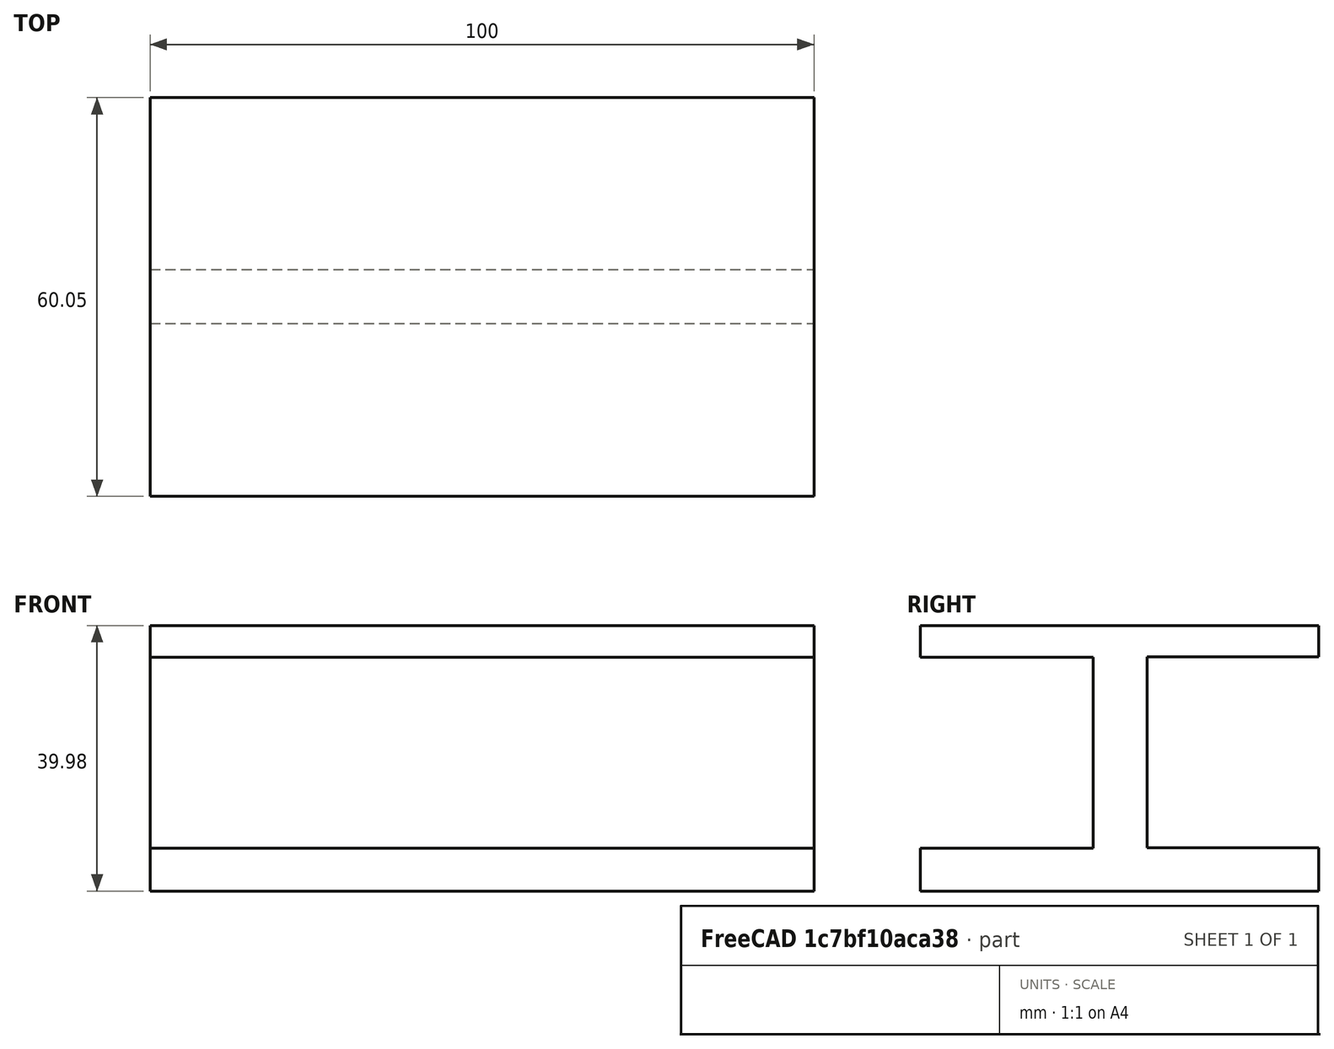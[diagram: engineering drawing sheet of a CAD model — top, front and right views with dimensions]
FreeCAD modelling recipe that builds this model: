
FCSTD DOCUMENT  (FreeCAD 0.21R33694 (Git))
Label: OJT1_T18R01_biga
License: All rights reserved
LicenseURL: https://en.wikipedia.org/wiki/All_rights_reserved
objects: Sketcher::SketchObject×1, PartDesign::Pad×1, PartDesign::Body×1
note: 4 computed .brp shape members not serialized (recipe doc carries the construction recipe); baked Part::Feature solids carry a one-line shape summary decoded from their .brp

FEATURE [Sketcher::SketchObject] Sketch
  FullyConstrained = false
  MapMode = 5
  Placement = pos=(0,0,0) rot=(0.57735,0.57735,0.57735;2.0944rad)
  Support = -> [YZ_Plane]
  sketch-geometry (12):
    g0: LineSegment StartX=-30.05 StartY=0 StartZ=0 EndX=29.9884 EndY=0 EndZ=0
    g1: LineSegment StartX=29.9884 StartY=0 StartZ=0 EndX=29.9884 EndY=6.48477 EndZ=0
    g2: LineSegment StartX=29.9884 StartY=6.48477 StartZ=0 EndX=4.08898 EndY=6.48477 EndZ=0
    g3: LineSegment StartX=4.08898 StartY=6.48477 StartZ=0 EndX=4.08898 EndY=35.2721 EndZ=0
    g4: LineSegment StartX=4.08898 StartY=35.2721 StartZ=0 EndX=29.9857 EndY=35.2721 EndZ=0
    g5: LineSegment StartX=29.9857 StartY=35.2721 StartZ=0 EndX=29.9857 EndY=39.985 EndZ=0
    g6: LineSegment StartX=29.9857 StartY=39.985 StartZ=0 EndX=-30.0648 EndY=39.985 EndZ=0
    g7: LineSegment StartX=-30.0648 StartY=39.985 StartZ=0 EndX=-30.0648 EndY=35.1993 EndZ=0
    g8: LineSegment StartX=-30.0648 StartY=35.1993 StartZ=0 EndX=-4.01671 EndY=35.1993 EndZ=0
    g9: LineSegment StartX=-4.01671 StartY=35.1993 StartZ=0 EndX=-4.01671 EndY=6.43061 EndZ=0
    g10: LineSegment StartX=-4.01671 StartY=6.43061 StartZ=0 EndX=-30.05 EndY=6.43061 EndZ=0
    g11: LineSegment StartX=-30.05 StartY=6.43061 StartZ=0 EndX=-30.05 EndY=0 EndZ=0
  constraints (25):
    c: PointOnObject(g0,g-1)
    c: Horizontal(g0)
    c: Coincident(g0,g1)
    c: Vertical(g1)
    c: Coincident(g1,g2)
    c: Horizontal(g2)
    c: Coincident(g2,g3)
    c: Vertical(g3)
    c: Coincident(g3,g4)
    c: Horizontal(g4)
    c: Coincident(g4,g5)
    c: Vertical(g5)
    c: Coincident(g5,g6)
    c: Horizontal(g6)
    c: Coincident(g6,g7)
    c: Vertical(g7)
    c: Coincident(g7,g8)
    c: Horizontal(g8)
    c: Coincident(g8,g9)
    c: Vertical(g9)
    c: Coincident(g9,g10)
    c: Horizontal(g10)
    c: Coincident(g10,g11)
    c: Coincident(g11,g0)
    c: Vertical(g11)
FEATURE [PartDesign::Pad] Pad
  Direction = (1,-2e-16,3e-16)
  Length = 100
  Length2 = 10
  Placement = pos=(0,0,0) rot=(1,1,1;2.0944rad)
  Profile = -> Sketch
  ReferenceAxis = -> Sketch [N_Axis]
  Type = 0
FEATURE [PartDesign::Body] Body
  Group = -> [Sketch,Pad]
  Origin = -> Origin
  Tip = -> Pad
